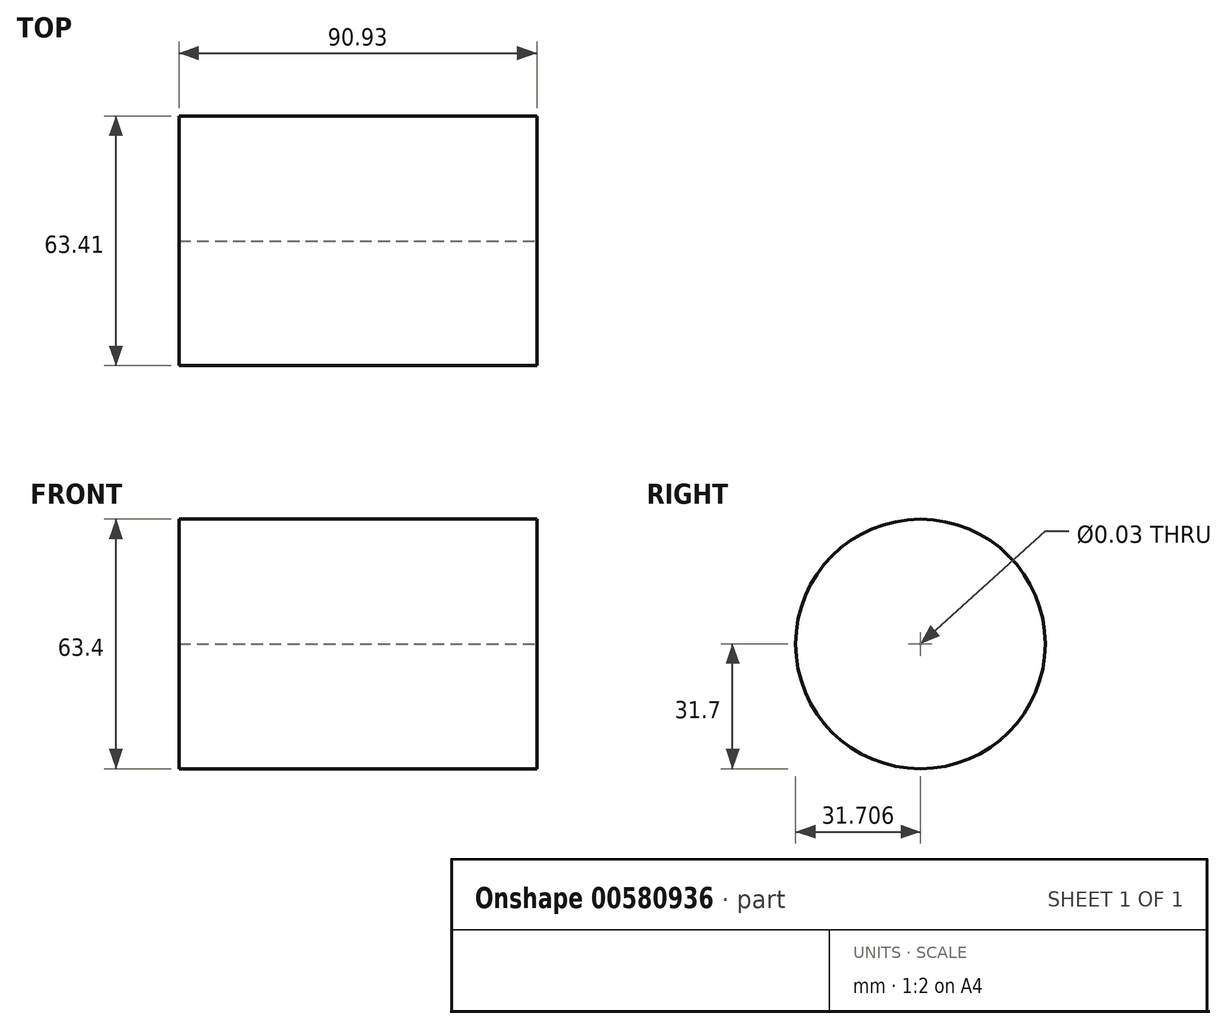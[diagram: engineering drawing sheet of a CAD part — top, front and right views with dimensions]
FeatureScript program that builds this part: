
annotation { "Feature Type Name" : "Feature", "Feature Type Description" : "" }
export const myFeature = defineFeature(function(context is Context, id is Id, definition is map)
    precondition{}
    {
        {
            var Q0;
            Q0=qCreatedBy(makeId("Right.planeOp"),FACE);
            var sketch = newSketch(context, id + "F0", { "sketchPlane" : qUnion([Q0])});
            skCircle(sketch, "E0", {"center": v(-73.63, 47.55) * mm, "radius": 31.7 * mm});
            skSolve(sketch);
        }
        {
            var Q0;
            Q0=makeQuery(id+"F0.imprint","IMPRINT",FACE,{"disambiguationData":[TD([[makeQuery(id+"F0.imprint","IMPRINT",EDGE,{"derivedFrom":sQuery(id+"F0.wireOp",EDGE,"E0")}),1.0]])]});
            extrude(context, id + "F1", {"entities" : qUnion([Q0]), "depth" : 90.93 * mm, "offsetDistance" : 25.4 * mm});
        }
        {
            var Q0;
            Q0=makeQuery(id+"F1.opExtrude","CAP_FACE",FACE,{"disambiguationData":[OSD([sQuery(id+"F0.wireOp",EDGE,"E0")])],"isStart":false});
            var sketch = newSketch(context, id + "F2", { "sketchPlane" : qUnion([Q0])});
            skCircle(sketch, "E1", {"center": v(-73.63, 47.55) * mm, "radius": 10.72 * mm});
            skSolve(sketch);
        }
        {
            var Q0;
            Q0=sQuery(id+"F2.wireOp",VERTEX,"E1.center");
            var Q1;
            Q1=makeQuery(id+"F1.opExtrude","SWEPT_BODY",BODY,{"disambiguationData":[OSD([sQuery(id+"F0.wireOp",EDGE,"E0")])]});
            hole(context, id + "F3", {"style" : HoleStyle.SIMPLE, "endStyle" : HoleEndStyle.THROUGH, "standardTappedOrClearance" : lookupTablePath({ "standard" : "ANSI", "size" : "27/32 (0.84)", "type" : "Drilled" }), "standardBlindInLast" : lookupTablePath({ "standard" : "ANSI", "size" : "27/32", "type" : "Drilled" }), "holeDiameter" : 27 / 812.8 * mm, "majorDiameter" : 6.35 * mm, "isTappedThrough" : true, "tappedDepth" : 12.7 * mm, "tapClearance" : 3, "locations" : qUnion([Q0]), "scope" : qUnion([Q1])});
        }
    });
